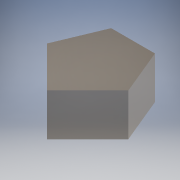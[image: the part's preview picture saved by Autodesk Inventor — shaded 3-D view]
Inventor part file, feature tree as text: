
AUTODESK INVENTOR PART (.ipt)
format: ipt  version: 2017 (Build 210142000, 142)  size: 99,328 bytes
history: native  units: mm
features: extrude x1, sketch x1
ambient origin geometry x8: Origin, YZ Plane, XZ Plane, XY Plane, X Axis, Y Axis, Z Axis, Center Point
bodies: Solid1 (feature_tree)
feature tree (2):
  extrude  "Extrusion1"  Depth=11.0mm
  sketch  "Sketch1"  dims[d0=90.0deg d1=112.5deg d2=112.5deg d3=112.5deg d4=15.0mm d5=12.805mm d6=11.0mm d7=0.0mm]
